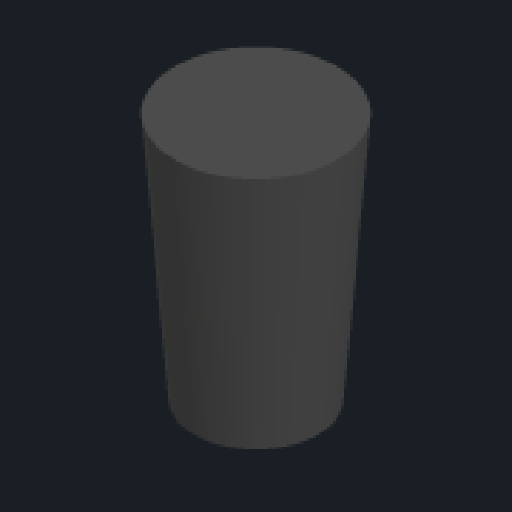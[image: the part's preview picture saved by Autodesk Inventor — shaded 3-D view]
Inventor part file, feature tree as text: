
AUTODESK INVENTOR PART (.ipt)
format: ipt  version: 2023.1 (Build 271208000, 208)  size: 101,376 bytes
history: native  units: mm
features: sketch x2, plane x2, loft x1
ambient origin geometry x8: Origin, YZ Plane, XZ Plane, XY Plane, X Axis, Y Axis, Z Axis, Center Point
bodies: Body1 (feature_tree)
feature tree (5):
  sketch  "Sketch1"  dims[d0=17.0mm d4=25.94mm]
  plane  "Work Plane1"
  plane  "Work Plane2"
  loft  "Loft1"
  sketch  "Sketch4"  dims[d5=13.0mm d6=0.0mm d7=90.0deg d8=0.0mm d9=90.0deg]
